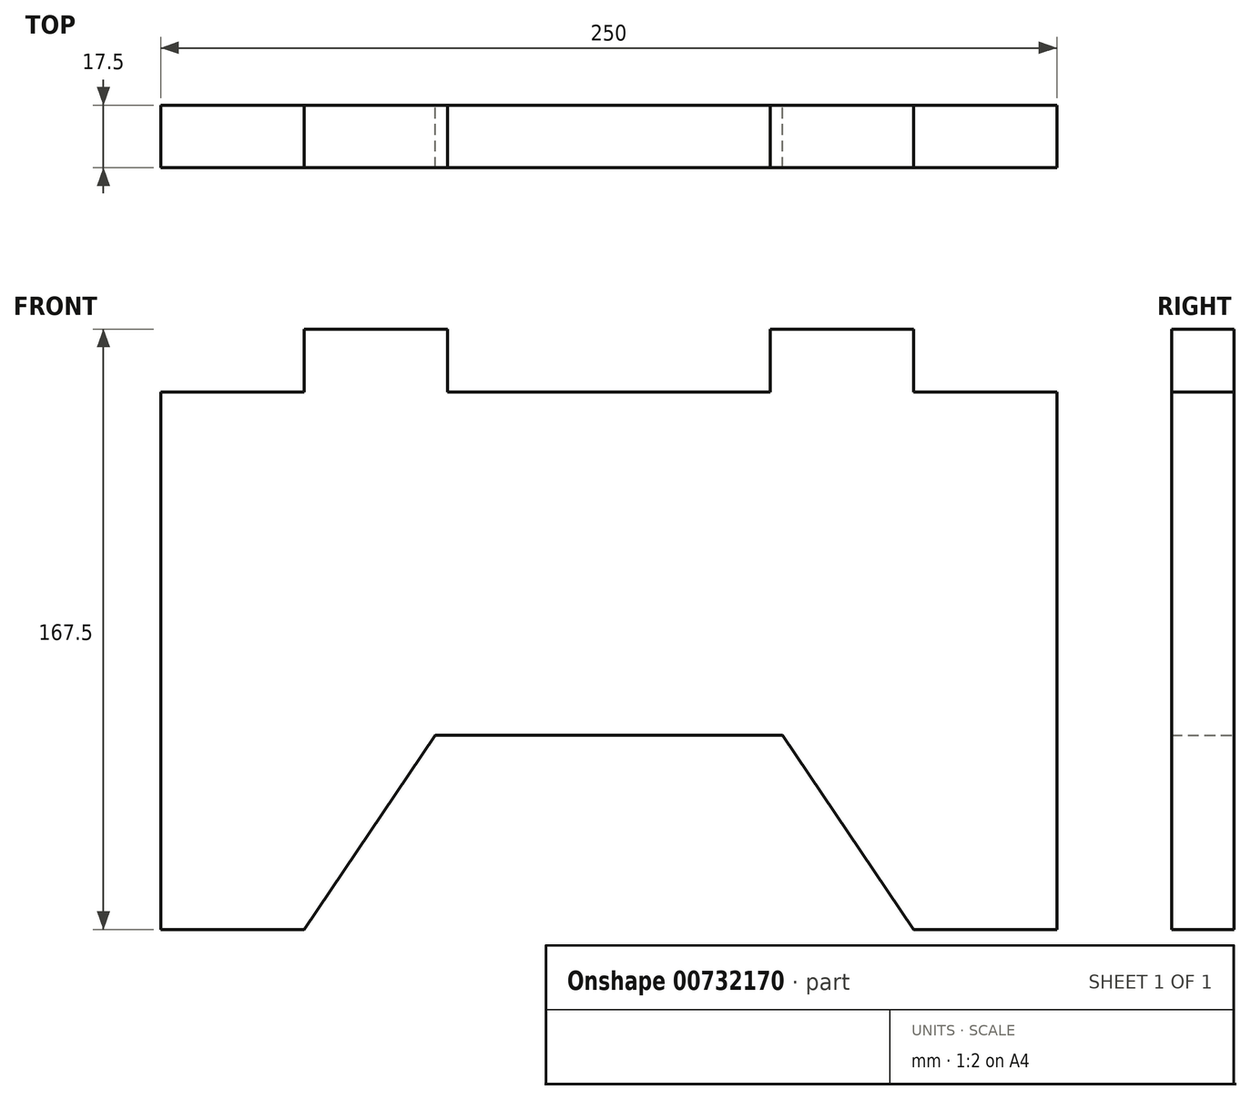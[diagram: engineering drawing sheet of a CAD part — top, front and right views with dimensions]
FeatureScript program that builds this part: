
annotation { "Feature Type Name" : "Feature", "Feature Type Description" : "" }
export const myFeature = defineFeature(function(context is Context, id is Id, definition is map)
    precondition{}
    {
        {
            var Q0;
            Q0=qCreatedBy(makeId("Front.planeOp"),FACE);
            var sketch = newSketch(context, id + "F0", { "sketchPlane" : qUnion([Q0])});
            skLineSegment(sketch, "E0.bottom", {"start": v(-122.62, 0) * mm, "end": v(-82.62, 0) * mm});
            skLineSegment(sketch, "E0.top", {"start": v(-122.62, 150) * mm, "end": v(-82.62, 150) * mm});
            skLineSegment(sketch, "E0.left", {"start": v(-122.62, 0) * mm, "end": v(-122.62, 150) * mm});
            skLineSegment(sketch, "E0.right", {"start": v(127.38, 0) * mm, "end": v(127.38, 150) * mm});
            skPoint(sketch, "E1.orphan", {"position": v(-122.62, 0) * mm});
            skLineSegment(sketch, "E2.top", {"start": v(-82.62, 167.5) * mm, "end": v(-42.62, 167.5) * mm});
            skLineSegment(sketch, "E2.left", {"start": v(-82.62, 150) * mm, "end": v(-82.62, 167.5) * mm});
            skLineSegment(sketch, "E2.right", {"start": v(-42.62, 150) * mm, "end": v(-42.62, 167.5) * mm});
            skLineSegment(sketch, "E3.top", {"start": v(47.38, 167.5) * mm, "end": v(87.38, 167.5) * mm});
            skLineSegment(sketch, "E3.left", {"start": v(47.38, 150) * mm, "end": v(47.38, 167.5) * mm});
            skLineSegment(sketch, "E3.right", {"start": v(87.38, 150) * mm, "end": v(87.38, 167.5) * mm});
            skLineSegment(sketch, "E4.trimOffspring", {"start": v(-42.62, 150) * mm, "end": v(47.38, 150) * mm});
            skLineSegment(sketch, "E5.trimOffspring", {"start": v(87.38, 150) * mm, "end": v(127.38, 150) * mm});
            skLineSegment(sketch, "E6", {"start": v(-82.62, 0) * mm, "end": v(-46.1, 54.15) * mm});
            skLineSegment(sketch, "E7", {"start": v(-46.1, 54.15) * mm, "end": v(50.86, 54.15) * mm});
            skLineSegment(sketch, "E8", {"start": v(50.86, 54.15) * mm, "end": v(87.38, 0) * mm});
            skLineSegment(sketch, "E9.trimOffspring", {"start": v(87.38, 0) * mm, "end": v(127.38, 0) * mm});
            skSolve(sketch);
        }
        {
            var Q0;
            Q0 = qSketchRegion(id + "F0", true);
            extrude(context, id + "F1", {"entities" : qUnion([Q0]), "depth" : 17.5 * mm, "offsetDistance" : 25 * mm});
        }
    });
